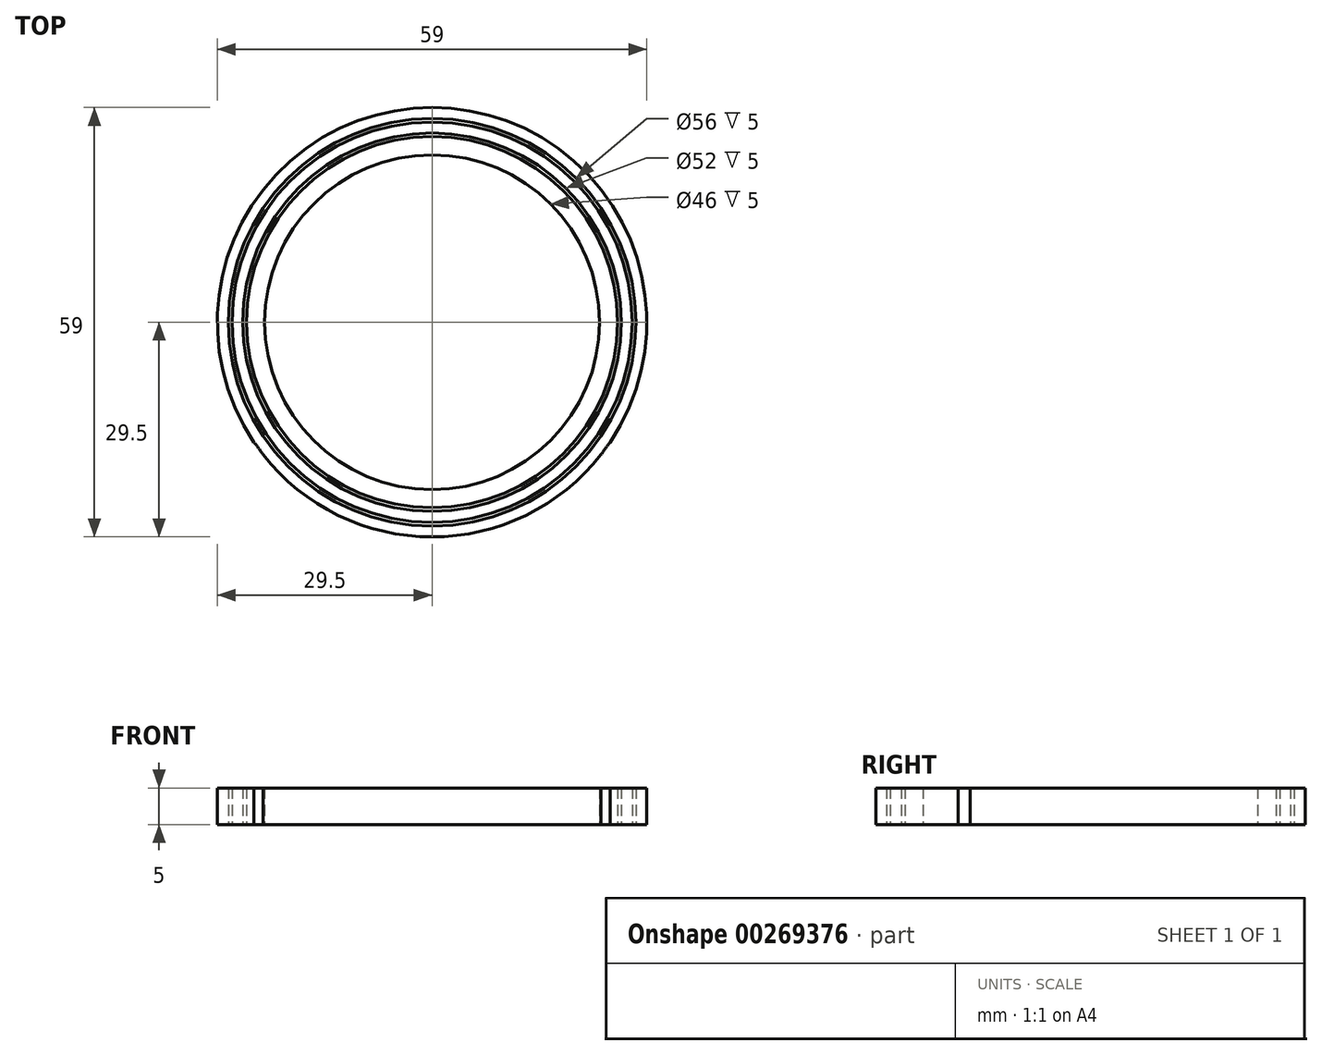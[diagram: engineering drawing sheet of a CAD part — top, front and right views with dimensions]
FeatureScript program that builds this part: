
annotation { "Feature Type Name" : "Feature", "Feature Type Description" : "" }
export const myFeature = defineFeature(function(context is Context, id is Id, definition is map)
    precondition{}
    {
        {
            var Q0;
            Q0=qCreatedBy(makeId("Top.planeOp"),FACE);
            var sketch = newSketch(context, id + "F0", { "sketchPlane" : qUnion([Q0])});
            skCircle(sketch, "E0", {"center": v(0, 60) * mm, "radius": 28 * mm});
            skCircle(sketch, "E1", {"center": v(0, 60) * mm, "radius": 27.5 * mm});
            skCircle(sketch, "E2", {"center": v(0, 60) * mm, "radius": 26 * mm});
            skCircle(sketch, "E3", {"center": v(0, 60) * mm, "radius": 23 * mm});
            skCircle(sketch, "E4", {"center": v(0, 60) * mm, "radius": 25.5 * mm});
            skCircle(sketch, "E5", {"center": v(0, 60) * mm, "radius": 29.5 * mm});
            skLineSegment(sketch, "E6", {"start": v(0, 138.92) * mm, "end": v(0, 0) * mm, "construction": true});
            skLineSegment(sketch, "E7", {"start": v(0, 0) * mm, "end": v(-104.44, -60.3) * mm, "construction": true});
            skLineSegment(sketch, "E8", {"start": v(0, 0) * mm, "end": v(110.38, -63.73) * mm, "construction": true});
            skCircle(sketch, "E9", {"center": v(-51.96, -30) * mm, "radius": 28 * mm});
            skCircle(sketch, "E10", {"center": v(-51.96, -30) * mm, "radius": 27.5 * mm});
            skCircle(sketch, "E11", {"center": v(-51.96, -30) * mm, "radius": 26 * mm});
            skCircle(sketch, "E12", {"center": v(-51.96, -30) * mm, "radius": 23 * mm});
            skCircle(sketch, "E13", {"center": v(-51.96, -30) * mm, "radius": 25.5 * mm});
            skCircle(sketch, "E14", {"center": v(-51.96, -30) * mm, "radius": 29.5 * mm});
            skCircle(sketch, "E15", {"center": v(51.96, -30) * mm, "radius": 28 * mm});
            skCircle(sketch, "E16", {"center": v(51.96, -30) * mm, "radius": 27.5 * mm});
            skCircle(sketch, "E17", {"center": v(51.96, -30) * mm, "radius": 26 * mm});
            skCircle(sketch, "E18", {"center": v(51.96, -30) * mm, "radius": 23 * mm});
            skCircle(sketch, "E19", {"center": v(51.96, -30) * mm, "radius": 25.5 * mm});
            skCircle(sketch, "E20", {"center": v(51.96, -30) * mm, "radius": 29.5 * mm});
            skLineSegment(sketch, "E21", {"start": v(-51.96, -30) * mm, "end": v(-83.4, 24.46) * mm, "construction": true});
            skPoint(sketch, "E22", {"position": v(-66.71, -4.45) * mm});
            skPoint(sketch, "E23", {"position": v(-29.5, 60) * mm});
            skArc(sketch, "E24", {"start": v(-49.9, -0.57) * mm, "mid": v(-22.25, 12.85) * mm, "end": v(-24.46, 43.5) * mm});
            skArc(sketch, "E25", {"start": v(24.46, 43.5) * mm, "mid": v(22.25, 12.85) * mm, "end": v(49.9, -0.57) * mm});
            skArc(sketch, "E26", {"start": v(25.45, -42.94) * mm, "mid": v(0, -25.7) * mm, "end": v(-25.45, -42.94) * mm});
            skSolve(sketch);
        }
        {
            var Q0;
            Q0=makeQuery(id+"F0.imprint","IMPRINT",FACE,{"disambiguationData":[TD([[makeQuery(id+"F0.imprint","IMPRINT",EDGE,{"derivedFrom":sQuery(id+"F0.wireOp",EDGE,"E0")}),-1.0]])]});
            var Q1;
            Q1=makeQuery(id+"F0.imprint","IMPRINT",FACE,{"disambiguationData":[TD([[makeQuery(id+"F0.imprint","IMPRINT",EDGE,{"derivedFrom":sQuery(id+"F0.wireOp",EDGE,"E3")}),-1.0]])]});
            var Q2;
            Q2=makeQuery(id+"F0.imprint","IMPRINT",FACE,{"disambiguationData":[TD([[makeQuery(id+"F0.imprint","IMPRINT",EDGE,{"derivedFrom":sQuery(id+"F0.wireOp",EDGE,"E1")}),1.0]])]});
            var Q3;
            Q3=makeQuery(id+"F0.imprint","IMPRINT",FACE,{"disambiguationData":[TD([[makeQuery(id+"F0.imprint","IMPRINT",EDGE,{"derivedFrom":sQuery(id+"F0.wireOp",EDGE,"ffb0c9cf-6b95-47ed-a45e-8d80741be1033.MirrorC")}),-1.0]])]});
            var Q4;
            Q4=makeQuery(id+"F0.imprint","IMPRINT",FACE,{"disambiguationData":[TD([[makeQuery(id+"F0.imprint","IMPRINT",EDGE,{"derivedFrom":sQuery(id+"F0.wireOp",EDGE,"ffb0c9cf-6b95-47ed-a45e-8d80741be1030.MirrorC")}),1.0]])]});
            extrude(context, id + "F1", {"entities" : qUnion([Q0, Q1, Q2, Q3, Q4]), "depth" : 5 * mm});
        }
    });
